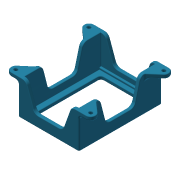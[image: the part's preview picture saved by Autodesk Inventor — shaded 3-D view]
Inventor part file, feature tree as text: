
AUTODESK INVENTOR PART (.ipt)
format: ipt  version: 2014 (Build 180170000, 170)  size: 620,032 bytes
history: native  units: mm
features: fillet x8, extrude x6, sketch x6, mirror x2
ambient origin geometry x8: Origin, YZ Plane, XZ Plane, XY Plane, X Axis, Y Axis, Z Axis, Center Point
bodies: Solid1 (feature_tree)
feature tree (22):
  extrude  "Extrusion1"  Depth=107.6mm
  extrude  "Extrusion2"  Depth=7.5mm
  extrude  "Extrusion3"  Depth=5.5mm
  extrude  "Extrusion4"  Depth=5.0mm
  mirror  "Mirror1"
  mirror  "Mirror2"
  extrude  "Extrusion5"  Depth=45.0mm TaperAngle=0.0deg
  extrude  "Extrusion6"  Depth=15.0mm
  fillet  "Fillet1"  Radius=65.0mm
  fillet  "Fillet2"  Radius=8.0mm
  fillet  "Fillet3"  Radius=4.5mm
  fillet  "Fillet4"  Radius=10.0mm
  fillet  "Fillet5"  Radius=7.0mm
  fillet  "Fillet6"  Radius=25.0mm
  fillet  "Fillet7"  Radius=6.0mm
  fillet  "Fillet8"  Radius=40.0mm
  sketch  "Sketch1"  dims[d0=76.2mm d1=107.6mm]
  sketch  "Sketch2"  dims[d2=7.5mm d3=7.5mm]
  sketch  "Sketch3"  dims[d4=5.5mm d5=5.5mm]
  sketch  "Sketch4"  dims[d6=5.0mm d7=0.0mm d8=5.0mm]
  sketch  "Sketch5"  dims[d9=5.0mm d10=45.0mm d11=0.0mm]
  sketch  "Sketch6"  dims[d12=40.0mm d13=15.0mm d14=65.0mm d15=8.0mm d16=0.0mm d17=4.5mm d18=10.0mm d19=7.0mm d20=25.0mm d21=6.0mm d22=0.0mm d23=40.0mm d24=58.0mm d25=6.0mm d26=0.0mm d27=2.5mm d28=2.5mm d29=2.9mm d30=0.0mm d31=8.0mm d32=4.0mm d33=1.0mm d34=1.0mm d35=1.0mm d36=2.0mm d37=1.0mm d38=0.5mm]
